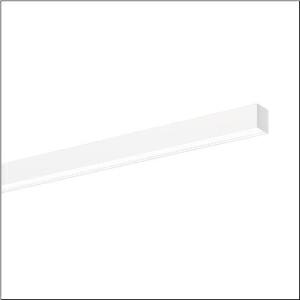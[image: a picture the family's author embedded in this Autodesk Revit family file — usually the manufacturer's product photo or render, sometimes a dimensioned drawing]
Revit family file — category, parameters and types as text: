
# Revit family: silica_r__21_51mx23da44wb_8e2d
name_source: partatom
category: Lighting Fixtures
units: mm (PartAtom-declared; Revit-internal decimal feet)

## family parameters
Cut with Voids When Loaded = No
Host = Face
Light Source = No
Part Type = Normal
Room Calculation Point = No
Round Connector Dimension = Use Diameter
Shared = No

## types (1)
- --- (1 x LED, 3280 lm, 22.4 W, 4000K)
    Apparent Load = 22 VA
    CIE Flux Codes = 78 96 99 100 100
    Color Rendering = 80
    Color Temperature = 4000K
    Default Elevation = 1800 mm
    Description = Silica® 21, office luminaire, primary optical cover: prismatic diffuser, of PMMA, CAT 2 (L<= 3000cd/m²), light emission: direct distribution, primary light characteristic: symmetric, installation type: surface-mounted, LED, rated luminous flux: 3.280lm, luminous efficacy: 146lm/W, light colour: 840, colour temperature: 4000K, with terminal, 3+2-pole, max. 2.5mm², mains connection: 220..240V, AC, 50/60Hz, rated input power: 22.4W, luminaire housing, of aluminium, traffic white (RAL 9016), length: 1.204mm, width: 53mm, height: 53mm, protection rating (complete): IP20, insulation class (complete): insulation class I (protective earthing), certification: CE, permissible operating ambient temperature: 0..+35°C, standard: EN 50419, packaging unit: 1 piece
    Height = 0 mm  [stored 0 ft]
    Lamp = 1 x LED
    Lamp Light Flux = 3280 lm
    Lamp Power = 22.4 W
    Lamp count = 1
    Length = 1204 mm
    Luminous efficacy = 146 lm/W
    Manufacturer = Siteco
    ModVariant = No
    Model = 51MX23DA44WB
    Mounting Place = Ceiling
    Mounting Type = Recessed
    Number of Poles = 1
    OnlyDefault = Yes
    Power Factor = 1
    Product Name = Silica® 21
    Product group = office luminaire | ceiling recessed
    ProductGroupID = 401
    Protection Class = Protection class I
    Protection Degree = IP 20
    RLX_Detail_Level = 1
    RLX_Emergency_Light_Flux = 0 lm
    RLX_Emergency_Type = 0
    RLX_Emergency_Type_DB = No
    RlxData = <blob elided: 18729 chars, md5=c994172b>
    Socket = socket
    Standby Power = 0 W
    System Light Flux = 3280 lm
    System Power = 22 W
    Type Comments = factory setting: luminous flux: 100 % | dim-lin: 254 | 323 mA
    Type Image = l_1313601.jpg
    URL = http://relux.com
    VarID = @adj_068443
    Voltage = 0 V
    Weight = 0.00 kg
    Width = 53 mm

note: [stored X ft] marks values corroborated as IEEE doubles in the binary element streams (Revit-internal decimal feet)

## geometry (parser evidence)
native form markers: Blend x4, Sweep x11
no freeform markers — native parametric forms only
